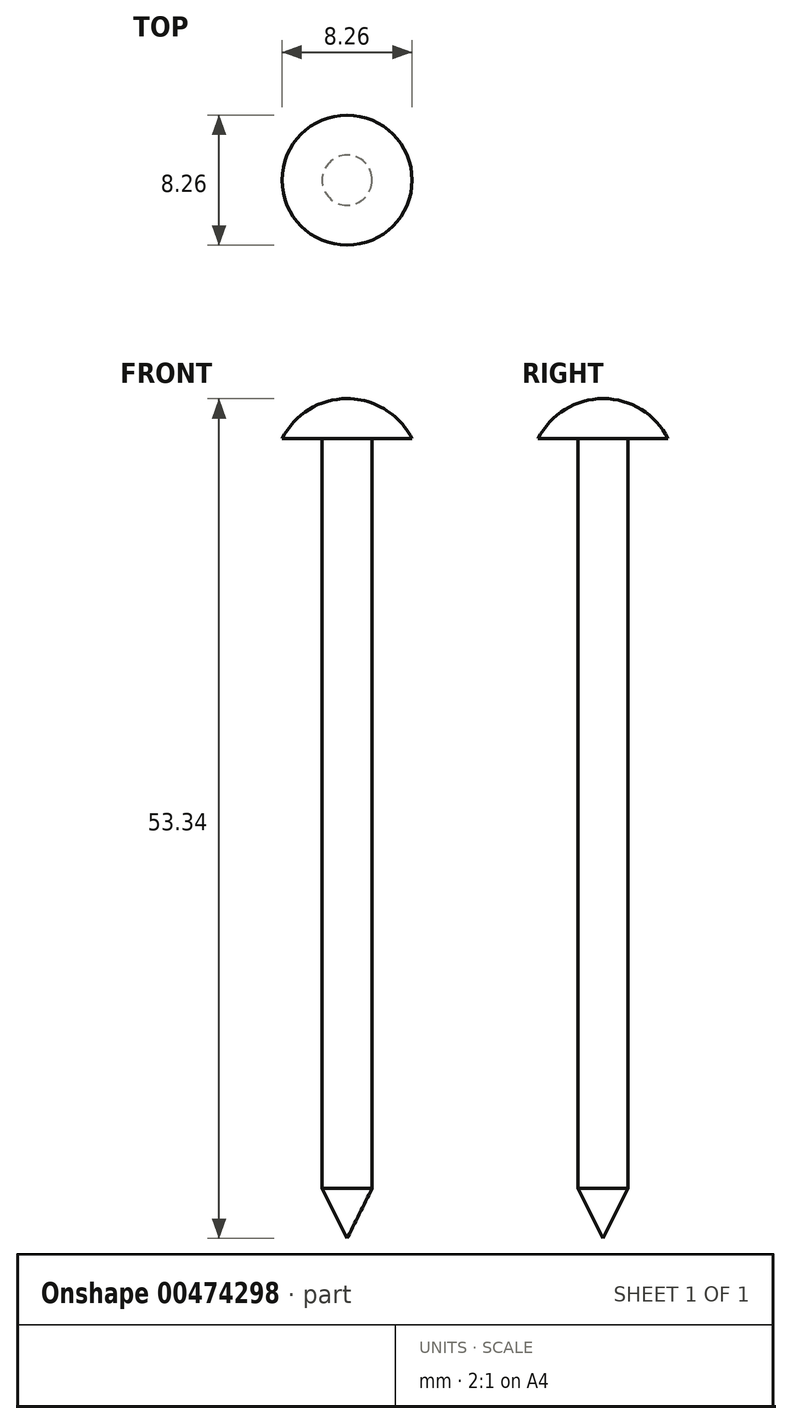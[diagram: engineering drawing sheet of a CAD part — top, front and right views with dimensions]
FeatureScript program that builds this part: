
annotation { "Feature Type Name" : "Feature", "Feature Type Description" : "" }
export const myFeature = defineFeature(function(context is Context, id is Id, definition is map)
    precondition{}
    {
        {
            var Q0;
            Q0=qCreatedBy(makeId("Front.planeOp"),FACE);
            var sketch = newSketch(context, id + "F0", { "sketchPlane" : qUnion([Q0])});
            skLineSegment(sketch, "E0", {"start": v(0, -50.8) * mm, "end": v(1.59, -47.62) * mm});
            skLineSegment(sketch, "E1", {"start": v(1.59, -47.63) * mm, "end": v(1.59, 0) * mm});
            skLineSegment(sketch, "E2", {"start": v(1.59, 0) * mm, "end": v(4.13, 0) * mm});
            skLineSegment(sketch, "E3", {"start": v(0, 2.54) * mm, "end": v(0, -50.8) * mm});
            skArc(sketch, "E4", {"start": v(4.13, 0) * mm, "mid": v(2.42, 1.85) * mm, "end": v(0, 2.54) * mm});
            skSolve(sketch);
        }
        {
            var Q0;
            Q0 = qSketchRegion(id + "F0", true);
            var Q1;
            Q1=sQuery(id+"F0.wireOp",EDGE,"E3");
            revolve(context, id + "F1", {"entities" : qUnion([Q0]), "axis" : qUnion([Q1]), "revolveType" : RevolveType.FULL});
        }
    });
